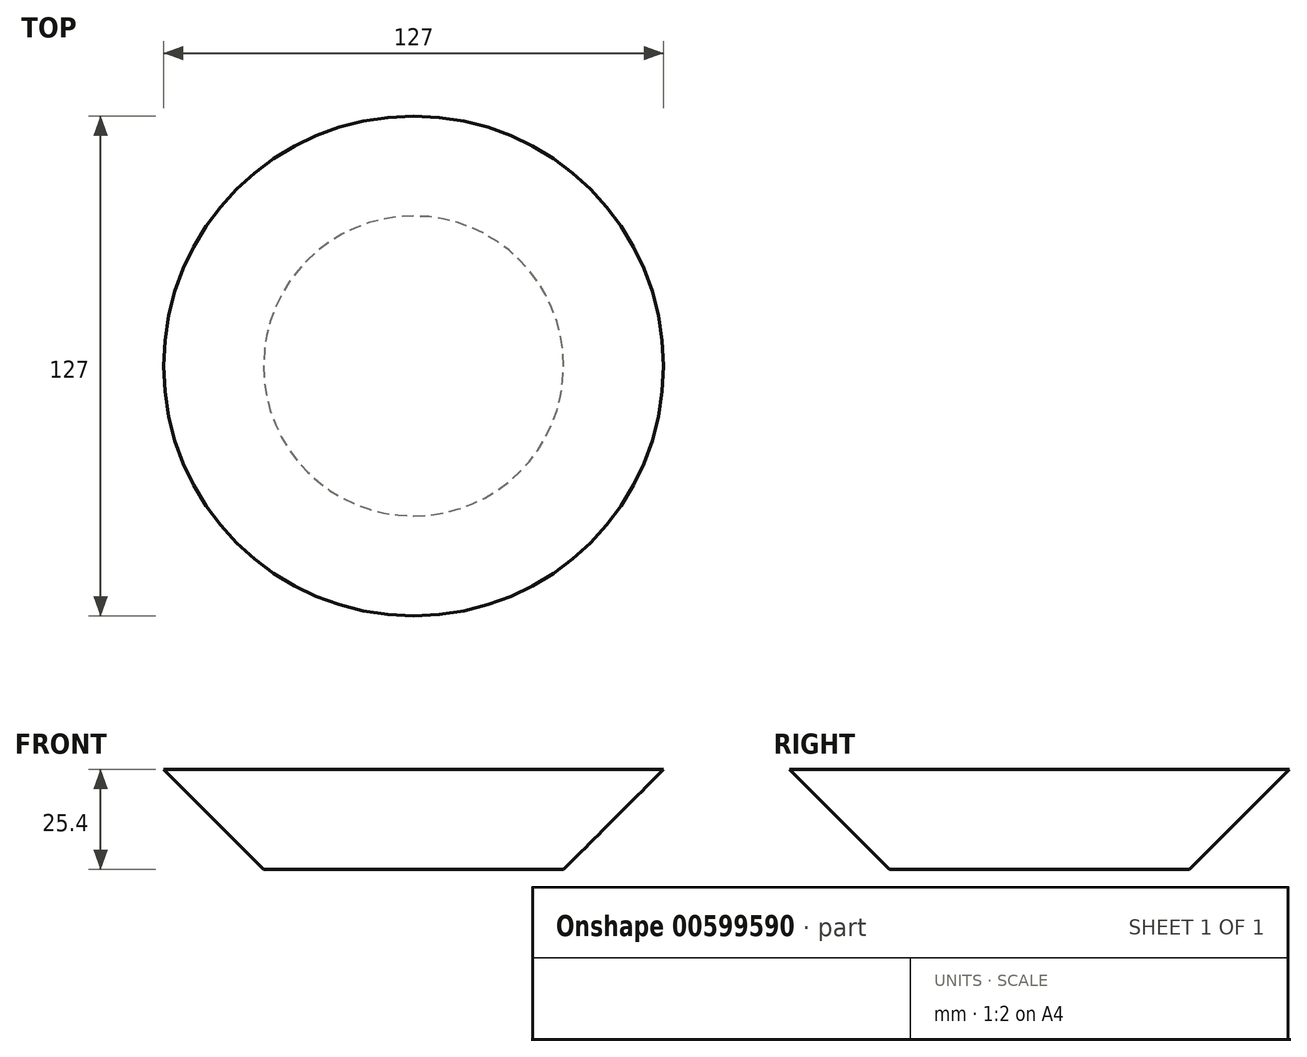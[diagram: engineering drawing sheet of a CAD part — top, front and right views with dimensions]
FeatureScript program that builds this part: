
annotation { "Feature Type Name" : "Feature", "Feature Type Description" : "" }
export const myFeature = defineFeature(function(context is Context, id is Id, definition is map)
    precondition{}
    {
        {
            var Q0;
            Q0=qCreatedBy(makeId("Top.planeOp"),FACE);
            var sketch = newSketch(context, id + "F0", { "sketchPlane" : qUnion([Q0])});
            skCircle(sketch, "E0", {"center": v(0, 0) * mm, "radius": 63.5 * mm});
            skSolve(sketch);
        }
        {
            var Q0;
            Q0=qCreatedBy(makeId("Top.planeOp"),FACE);
            cPlane(context, id + "F1", {"entities" : qUnion([Q0]), "cplaneType" : CPlaneType.OFFSET, "offset" : 25.4 * mm, "oppositeDirection" : true, "width" : 152.4 * mm, "height" : 152.4 * mm});
        }
        {
            var Q0;
            Q0=qCreatedBy(id+"F1.planeOp",FACE);
            var sketch = newSketch(context, id + "F2", { "sketchPlane" : qUnion([Q0])});
            skCircle(sketch, "E1.0", {"center": v(0, 0) * mm, "radius": 38.1 * mm});
            skSolve(sketch);
        }
        {
            var Q0;
            Q0=makeQuery(id+"F0.imprint","IMPRINT",FACE,{"disambiguationData":[TD([[makeQuery(id+"F0.imprint","IMPRINT",EDGE,{"derivedFrom":sQuery(id+"F0.wireOp",EDGE,"E0")}),1.0]])]});
            var Q1;
            Q1=makeQuery(id+"F2.imprint","IMPRINT",FACE,{"disambiguationData":[TD([[makeQuery(id+"F2.imprint","IMPRINT",EDGE,{"derivedFrom":sQuery(id+"F2.wireOp",EDGE,"E1.0")}),1.0]])]});
            loft(context, id + "F3", {"sheetProfilesArray" : [{ "sheetProfileEntities" : qUnion([Q0]) }, { "sheetProfileEntities" : qUnion([Q1]) }]});
        }
    });
